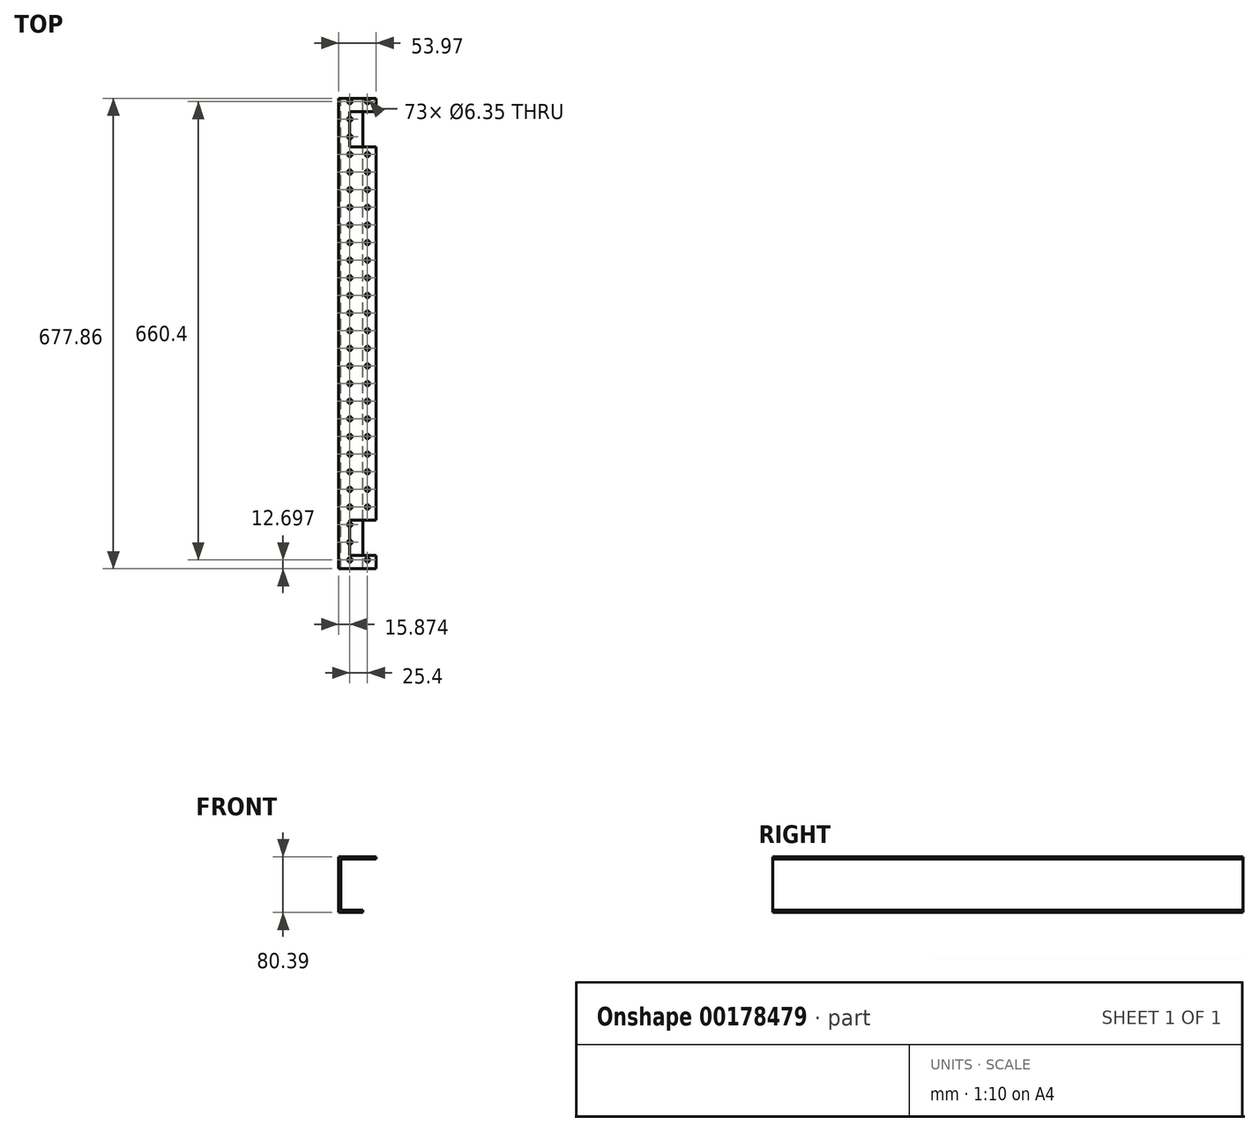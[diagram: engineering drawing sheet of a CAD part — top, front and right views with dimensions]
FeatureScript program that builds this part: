
annotation { "Feature Type Name" : "Feature", "Feature Type Description" : "" }
export const myFeature = defineFeature(function(context is Context, id is Id, definition is map)
    precondition{}
    {
        {
            var Q0;
            Q0=qCreatedBy(makeId("Front.planeOp"),FACE);
            var sketch = newSketch(context, id + "F0", { "sketchPlane" : qUnion([Q0])});
            skLineSegment(sketch, "E0", {"start": v(-48.66, 57.12) * mm, "end": v(-48.66, -23.27) * mm});
            skLineSegment(sketch, "E1", {"start": v(-48.66, 57.12) * mm, "end": v(5.31, 57.12) * mm});
            skLineSegment(sketch, "E2", {"start": v(-48.66, -23.27) * mm, "end": v(-13.74, -23.27) * mm});
            skLineSegment(sketch, "E3", {"start": v(-13.74, -23.27) * mm, "end": v(-13.74, -20.1) * mm});
            skLineSegment(sketch, "E4", {"start": v(-13.74, -20.1) * mm, "end": v(-45.49, -20.1) * mm});
            skLineSegment(sketch, "E5", {"start": v(-45.49, -20.1) * mm, "end": v(-45.49, 53.95) * mm});
            skLineSegment(sketch, "E6", {"start": v(-45.49, 53.95) * mm, "end": v(5.31, 53.95) * mm});
            skLineSegment(sketch, "E7", {"start": v(5.31, 53.95) * mm, "end": v(5.31, 57.12) * mm});
            skSolve(sketch);
        }
        {
            var Q0;
            Q0=makeQuery(id+"F0.imprint","IMPRINT",FACE,{"disambiguationData":[TD([[makeQuery(id+"F0.imprint","IMPRINT",EDGE,{"derivedFrom":sQuery(id+"F0.wireOp",EDGE,"E0")}),1.0]])]});
            var Q1;
            Q1=sQuery(id+"F0.wireOp",EDGE,"E0");
            var Q2;
            Q2=sQuery(id+"F0.wireOp",EDGE,"E1");
            var Q3;
            Q3=sQuery(id+"F0.wireOp",EDGE,"E2");
            var Q4;
            Q4=sQuery(id+"F0.wireOp",EDGE,"E3");
            var Q5;
            Q5=sQuery(id+"F0.wireOp",EDGE,"E4");
            var Q6;
            Q6=sQuery(id+"F0.wireOp",EDGE,"E5");
            var Q7;
            Q7=sQuery(id+"F0.wireOp",EDGE,"E6");
            var Q8;
            Q8=sQuery(id+"F0.wireOp",EDGE,"E7");
            extrude(context, id + "F1", {"entities" : qUnion([Q0]), "surfaceEntities" : qUnion([Q1, Q2, Q3, Q4, Q5, Q6, Q7, Q8]), "depth" : 677.86 * mm});
        }
        {
            var Q0;
            Q0=makeQuery(id+"F1.opExtrude","SWEPT_FACE",FACE,{"disambiguationData":[OSD([sQuery(id+"F0.wireOp",EDGE,"E6")])]});
            var sketch = newSketch(context, id + "F2", { "sketchPlane" : qUnion([Q0])});
            skLineSegment(sketch, "E8.bottom", {"start": v(5.31, 19.05) * mm, "end": v(-32.79, 19.05) * mm});
            skLineSegment(sketch, "E8.top", {"start": v(5.31, 69.85) * mm, "end": v(-32.79, 69.85) * mm});
            skLineSegment(sketch, "E8.left", {"start": v(5.31, 19.05) * mm, "end": v(5.31, 69.85) * mm});
            skLineSegment(sketch, "E8.right", {"start": v(-32.79, 19.05) * mm, "end": v(-32.79, 69.85) * mm});
            skLineSegment(sketch, "E9.bottom", {"start": v(5.31, 658.81) * mm, "end": v(-32.79, 658.81) * mm});
            skLineSegment(sketch, "E9.top", {"start": v(5.31, 608.01) * mm, "end": v(-32.79, 608.01) * mm});
            skLineSegment(sketch, "E9.left", {"start": v(5.31, 658.81) * mm, "end": v(5.31, 608.01) * mm});
            skLineSegment(sketch, "E9.right", {"start": v(-32.79, 658.81) * mm, "end": v(-32.79, 608.01) * mm});
            skSolve(sketch);
        }
        {
            var Q0;
            Q0 = qSketchRegion(id + "F2", true);
            extrude(context, id + "F3", {"entities" : qUnion([Q0]), "operationType" : NewBodyOperationType.REMOVE, "oppositeDirection" : true, "depth" : 25.4 * mm});
        }
        {
            var Q0;
            Q0=makeQuery(id+"F1.opExtrude","SWEPT_FACE",FACE,{"disambiguationData":[OSD([sQuery(id+"F0.wireOp",EDGE,"E1")])]});
            var sketch = newSketch(context, id + "F4", { "sketchPlane" : qUnion([Q0])});
            skCircle(sketch, "E10", {"center": v(-7.39, -665.16) * mm, "radius": 3.18 * mm});
            skCircle(sketch, "E11.0.1.0", {"center": v(-7.39, -639.76) * mm, "radius": 3.18 * mm});
            skCircle(sketch, "E11.0.2.0", {"center": v(-7.39, -614.36) * mm, "radius": 3.18 * mm});
            skCircle(sketch, "E11.0.3.0", {"center": v(-7.39, -588.96) * mm, "radius": 3.18 * mm});
            skCircle(sketch, "E11.0.4.0", {"center": v(-7.39, -563.56) * mm, "radius": 3.18 * mm});
            skCircle(sketch, "E11.0.5.0", {"center": v(-7.39, -538.16) * mm, "radius": 3.18 * mm});
            skCircle(sketch, "E11.0.6.0", {"center": v(-7.39, -512.76) * mm, "radius": 3.18 * mm});
            skCircle(sketch, "E11.0.7.0", {"center": v(-7.39, -487.36) * mm, "radius": 3.18 * mm});
            skCircle(sketch, "E11.0.8.0", {"center": v(-7.39, -461.96) * mm, "radius": 3.18 * mm});
            skCircle(sketch, "E11.0.9.0", {"center": v(-7.39, -436.56) * mm, "radius": 3.18 * mm});
            skCircle(sketch, "E11.0.10.0", {"center": v(-7.39, -411.16) * mm, "radius": 3.18 * mm});
            skCircle(sketch, "E11.0.11.0", {"center": v(-7.39, -385.76) * mm, "radius": 3.18 * mm});
            skCircle(sketch, "E11.0.12.0", {"center": v(-7.39, -360.36) * mm, "radius": 3.18 * mm});
            skCircle(sketch, "E11.0.13.0", {"center": v(-7.39, -334.96) * mm, "radius": 3.18 * mm});
            skCircle(sketch, "E11.0.14.0", {"center": v(-7.39, -309.56) * mm, "radius": 3.18 * mm});
            skCircle(sketch, "E11.0.15.0", {"center": v(-7.39, -284.16) * mm, "radius": 3.18 * mm});
            skCircle(sketch, "E11.0.16.0", {"center": v(-7.39, -258.76) * mm, "radius": 3.18 * mm});
            skCircle(sketch, "E11.0.17.0", {"center": v(-7.39, -233.36) * mm, "radius": 3.18 * mm});
            skCircle(sketch, "E11.0.18.0", {"center": v(-7.39, -207.96) * mm, "radius": 3.18 * mm});
            skCircle(sketch, "E11.0.19.0", {"center": v(-7.39, -182.56) * mm, "radius": 3.18 * mm});
            skCircle(sketch, "E11.0.20.0", {"center": v(-7.39, -157.16) * mm, "radius": 3.18 * mm});
            skCircle(sketch, "E11.0.21.0", {"center": v(-7.39, -131.76) * mm, "radius": 3.18 * mm});
            skCircle(sketch, "E11.0.22.0", {"center": v(-7.39, -106.36) * mm, "radius": 3.18 * mm});
            skCircle(sketch, "E11.0.23.0", {"center": v(-7.39, -80.96) * mm, "radius": 3.18 * mm});
            skCircle(sketch, "E11.0.24.0", {"center": v(-7.39, -55.56) * mm, "radius": 3.18 * mm});
            skCircle(sketch, "E11.0.25.0", {"center": v(-7.39, -30.16) * mm, "radius": 3.18 * mm});
            skCircle(sketch, "E11.0.26.0", {"center": v(-7.39, -4.76) * mm, "radius": 3.18 * mm});
            skCircle(sketch, "E11.1.0.0", {"center": v(-32.79, -665.16) * mm, "radius": 3.18 * mm});
            skCircle(sketch, "E11.1.1.0", {"center": v(-32.79, -639.76) * mm, "radius": 3.18 * mm});
            skCircle(sketch, "E11.1.2.0", {"center": v(-32.79, -614.36) * mm, "radius": 3.18 * mm});
            skCircle(sketch, "E11.1.3.0", {"center": v(-32.79, -588.96) * mm, "radius": 3.18 * mm});
            skCircle(sketch, "E11.1.4.0", {"center": v(-32.79, -563.56) * mm, "radius": 3.18 * mm});
            skCircle(sketch, "E11.1.5.0", {"center": v(-32.79, -538.16) * mm, "radius": 3.18 * mm});
            skCircle(sketch, "E11.1.6.0", {"center": v(-32.79, -512.76) * mm, "radius": 3.18 * mm});
            skCircle(sketch, "E11.1.7.0", {"center": v(-32.79, -487.36) * mm, "radius": 3.18 * mm});
            skCircle(sketch, "E11.1.8.0", {"center": v(-32.79, -461.96) * mm, "radius": 3.18 * mm});
            skCircle(sketch, "E11.1.9.0", {"center": v(-32.79, -436.56) * mm, "radius": 3.18 * mm});
            skCircle(sketch, "E11.1.10.0", {"center": v(-32.79, -411.16) * mm, "radius": 3.18 * mm});
            skCircle(sketch, "E11.1.11.0", {"center": v(-32.79, -385.76) * mm, "radius": 3.18 * mm});
            skCircle(sketch, "E11.1.12.0", {"center": v(-32.79, -360.36) * mm, "radius": 3.18 * mm});
            skCircle(sketch, "E11.1.13.0", {"center": v(-32.79, -334.96) * mm, "radius": 3.18 * mm});
            skCircle(sketch, "E11.1.14.0", {"center": v(-32.79, -309.56) * mm, "radius": 3.18 * mm});
            skCircle(sketch, "E11.1.15.0", {"center": v(-32.79, -284.16) * mm, "radius": 3.18 * mm});
            skCircle(sketch, "E11.1.16.0", {"center": v(-32.79, -258.76) * mm, "radius": 3.18 * mm});
            skCircle(sketch, "E11.1.17.0", {"center": v(-32.79, -233.36) * mm, "radius": 3.18 * mm});
            skCircle(sketch, "E11.1.18.0", {"center": v(-32.79, -207.96) * mm, "radius": 3.18 * mm});
            skCircle(sketch, "E11.1.19.0", {"center": v(-32.79, -182.56) * mm, "radius": 3.18 * mm});
            skCircle(sketch, "E11.1.20.0", {"center": v(-32.79, -157.16) * mm, "radius": 3.18 * mm});
            skCircle(sketch, "E11.1.21.0", {"center": v(-32.79, -131.76) * mm, "radius": 3.18 * mm});
            skCircle(sketch, "E11.1.22.0", {"center": v(-32.79, -106.36) * mm, "radius": 3.18 * mm});
            skCircle(sketch, "E11.1.23.0", {"center": v(-32.79, -80.96) * mm, "radius": 3.18 * mm});
            skCircle(sketch, "E11.1.24.0", {"center": v(-32.79, -55.56) * mm, "radius": 3.18 * mm});
            skCircle(sketch, "E11.1.25.0", {"center": v(-32.79, -30.16) * mm, "radius": 3.18 * mm});
            skCircle(sketch, "E11.1.26.0", {"center": v(-32.79, -4.76) * mm, "radius": 3.18 * mm});
            skLineSegment(sketch, "E11.direction1", {"start": v(-7.39, -665.16) * mm, "end": v(-32.79, -665.16) * mm, "construction": true});
            skLineSegment(sketch, "E11.direction2", {"start": v(-7.39, -665.16) * mm, "end": v(-7.39, -639.76) * mm, "construction": true});
            skSolve(sketch);
        }
        {
            var Q0;
            Q0 = qSketchRegion(id + "F4", true);
            extrude(context, id + "F5", {"entities" : qUnion([Q0]), "operationType" : NewBodyOperationType.REMOVE, "oppositeDirection" : true, "depth" : 101.6 * mm});
        }
    });
